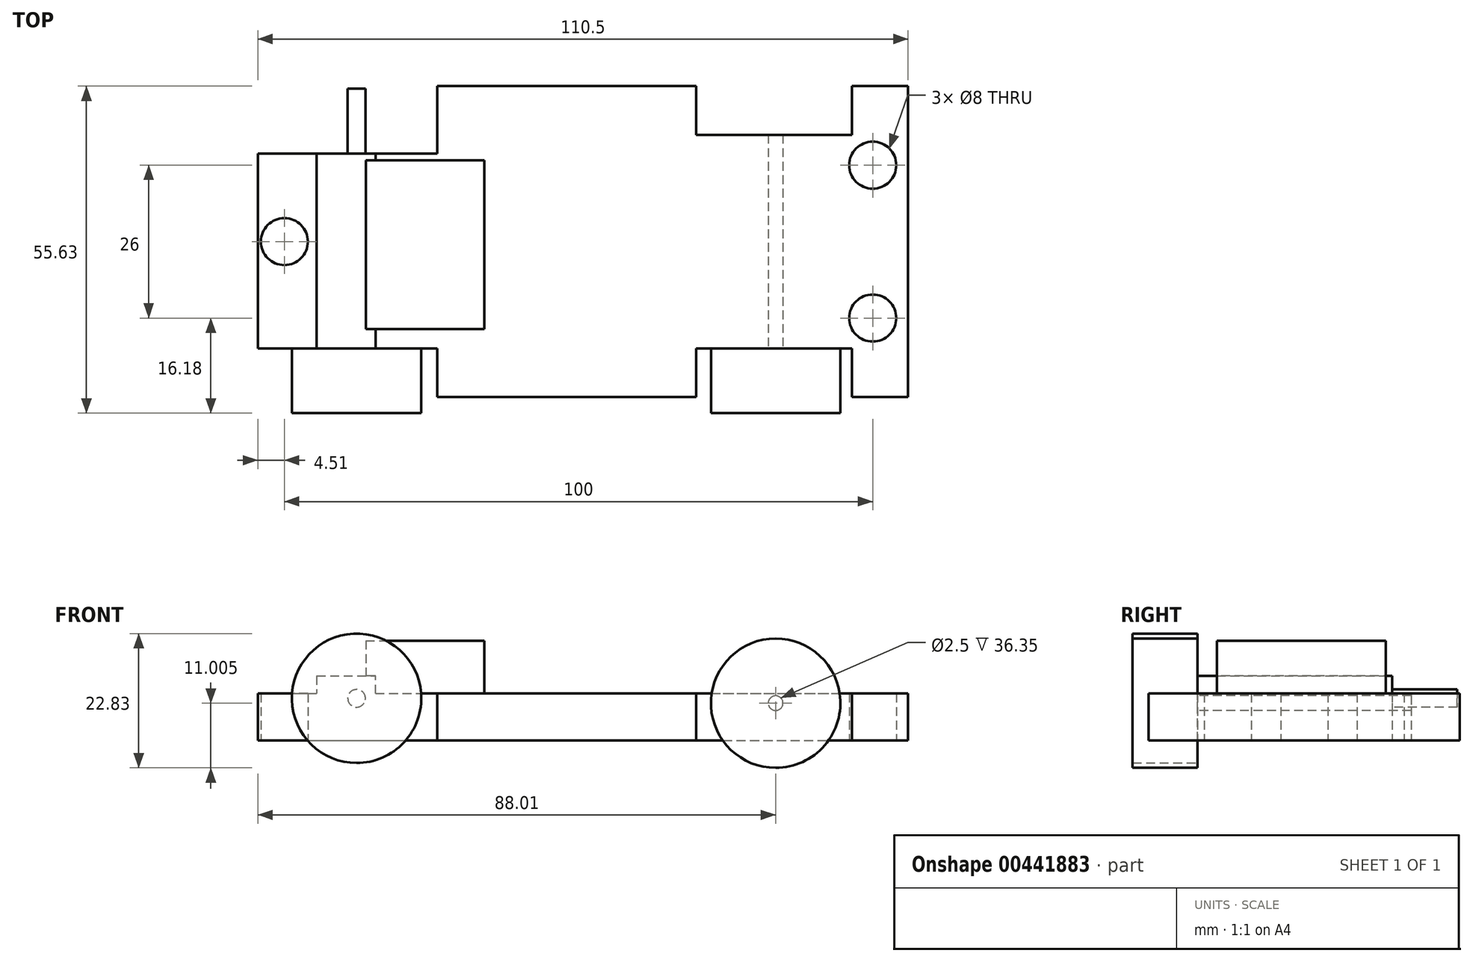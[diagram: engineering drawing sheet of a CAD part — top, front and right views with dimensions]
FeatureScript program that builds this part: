
annotation { "Feature Type Name" : "Feature", "Feature Type Description" : "" }
export const myFeature = defineFeature(function(context is Context, id is Id, definition is map)
    precondition{}
    {
        {
            var Q0;
            Q0=qCreatedBy(makeId("Top.planeOp"),FACE);
            var sketch = newSketch(context, id + "F0", { "sketchPlane" : qUnion([Q0])});
            skLineSegment(sketch, "E0.bottom", {"start": v(55.25, 26.46) * mm, "end": v(45.74, 26.46) * mm});
            skLineSegment(sketch, "E0.top", {"start": v(55.25, -26.46) * mm, "end": v(45.74, -26.46) * mm});
            skLineSegment(sketch, "E0.left", {"start": v(55.25, 26.46) * mm, "end": v(55.25, -26.46) * mm});
            skLineSegment(sketch, "E0.right", {"start": v(-55.25, 14.95) * mm, "end": v(-55.25, -18.18) * mm});
            skPoint(sketch, "E0.middle", {"position": v(0, 0) * mm});
            skCircle(sketch, "E1", {"center": v(-50.74, 0) * mm, "radius": 4 * mm});
            skCircle(sketch, "E2", {"center": v(49.26, 13) * mm, "radius": 4 * mm});
            skCircle(sketch, "E3.MirrorC", {"center": v(49.26, -13) * mm, "radius": 4 * mm});
            skLineSegment(sketch, "E4.top", {"start": v(-55.25, 14.95) * mm, "end": v(-24.73, 14.96) * mm});
            skLineSegment(sketch, "E4.right", {"start": v(-24.73, 26.45) * mm, "end": v(-24.73, 14.96) * mm});
            skLineSegment(sketch, "E5.top", {"start": v(-55.25, -18.18) * mm, "end": v(-24.75, -18.18) * mm});
            skLineSegment(sketch, "E5.right", {"start": v(-24.75, -26.46) * mm, "end": v(-24.75, -18.18) * mm});
            skLineSegment(sketch, "E6.top", {"start": v(19.25, 18.18) * mm, "end": v(45.74, 18.18) * mm});
            skLineSegment(sketch, "E6.left", {"start": v(19.25, 26.46) * mm, "end": v(19.25, 18.18) * mm});
            skLineSegment(sketch, "E6.right", {"start": v(45.74, 26.46) * mm, "end": v(45.74, 18.18) * mm});
            skLineSegment(sketch, "E7.MirrorCS", {"start": v(19.25, -18.18) * mm, "end": v(45.74, -18.18) * mm});
            skLineSegment(sketch, "E8.MirrorCS", {"start": v(19.25, -26.46) * mm, "end": v(19.25, -18.18) * mm});
            skLineSegment(sketch, "E9.MirrorCS", {"start": v(45.74, -26.46) * mm, "end": v(45.74, -18.18) * mm});
            skPoint(sketch, "E10.orphan", {"position": v(-55.25, 26.46) * mm});
            skPoint(sketch, "E11.orphan", {"position": v(-55.25, -26.46) * mm});
            skLineSegment(sketch, "E12.trimOffspring", {"start": v(19.25, -26.46) * mm, "end": v(-24.75, -26.46) * mm});
            skLineSegment(sketch, "E13.trimOffspring", {"start": v(19.25, 26.46) * mm, "end": v(-24.73, 26.46) * mm});
            skSolve(sketch);
        }
        {
            var Q0;
            Q0=qSketchRegion(id+"F0",true);
            extrude(context, id + "F1", {"entities" : qUnion([Q0]), "depth" : 8 * mm});
        }
        {
            var Q0;
            Q0=makeQuery(id+"F1.opExtrude","CAP_FACE",FACE,{"disambiguationData":[OSD([sQuery(id+"F0.wireOp",EDGE,"E0.bottom"),sQuery(id+"F0.wireOp",EDGE,"E0.top"),sQuery(id+"F0.wireOp",EDGE,"E0.left"),sQuery(id+"F0.wireOp",EDGE,"E0.right"),sQuery(id+"F0.wireOp",EDGE,"E1"),sQuery(id+"F0.wireOp",EDGE,"E2"),sQuery(id+"F0.wireOp",EDGE,"E3.MirrorC"),sQuery(id+"F0.wireOp",EDGE,"E4.top"),sQuery(id+"F0.wireOp",EDGE,"E4.right"),sQuery(id+"F0.wireOp",EDGE,"E5.top"),sQuery(id+"F0.wireOp",EDGE,"E5.right"),sQuery(id+"F0.wireOp",EDGE,"E6.top"),sQuery(id+"F0.wireOp",EDGE,"E6.left"),sQuery(id+"F0.wireOp",EDGE,"E6.right"),sQuery(id+"F0.wireOp",EDGE,"E7.MirrorCS"),sQuery(id+"F0.wireOp",EDGE,"E8.MirrorCS"),sQuery(id+"F0.wireOp",EDGE,"E9.MirrorCS"),sQuery(id+"F0.wireOp",EDGE,"E12.trimOffspring"),sQuery(id+"F0.wireOp",EDGE,"E13.trimOffspring")])],"isStart":false});
            var sketch = newSketch(context, id + "F2", { "sketchPlane" : qUnion([Q0])});
            skLineSegment(sketch, "E14.bottom", {"start": v(-45.25, 14.95) * mm, "end": v(-35.25, 14.96) * mm});
            skLineSegment(sketch, "E14.top", {"start": v(-45.25, -18.18) * mm, "end": v(-35.25, -18.18) * mm});
            skLineSegment(sketch, "E14.left", {"start": v(-45.25, 14.95) * mm, "end": v(-45.25, -18.18) * mm});
            skLineSegment(sketch, "E14.right", {"start": v(-35.25, 14.96) * mm, "end": v(-35.25, -18.18) * mm});
            skSolve(sketch);
        }
        {
            var Q0;
            Q0=qSketchRegion(id+"F2",true);
            extrude(context, id + "F3", {"entities" : qUnion([Q0]), "operationType" : NewBodyOperationType.ADD, "depth" : 3 * mm});
        }
        {
            var Q0;
            Q0=qCreatedBy(makeId("Front.planeOp"),FACE);
            var sketch = newSketch(context, id + "F4", { "sketchPlane" : qUnion([Q0])});
            skCircle(sketch, "E15", {"center": v(-38.47, 7.2) * mm, "radius": 1.5 * mm});
            skSolve(sketch);
        }
        {
            var Q0;
            Q0=qSketchRegion(id+"F4",true);
            extrude(context, id + "F5", {"entities" : qUnion([Q0]), "operationType" : NewBodyOperationType.ADD, "endBound" : BoundingType.SYMMETRIC, "oppositeDirection" : true, "depth" : 52 * mm});
        }
        {
            var Q0;
            {var subQ0=sQuery(id+"F0.wireOp",EDGE,"E6.top");var subQ1=sQuery(id+"F0.wireOp",EDGE,"E12.trimOffspring");var subQ2=sQuery(id+"F0.wireOp",EDGE,"E13.trimOffspring");var subQ3=sQuery(id+"F0.wireOp",EDGE,"E5.right");var subQ4=sQuery(id+"F0.wireOp",EDGE,"E5.top");var subQ5=sQuery(id+"F0.wireOp",EDGE,"E9.MirrorCS");var subQ6=sQuery(id+"F0.wireOp",EDGE,"E4.top");var subQ7=sQuery(id+"F0.wireOp",EDGE,"E7.MirrorCS");var subQ8=sQuery(id+"F0.wireOp",EDGE,"E3.MirrorC");var subQ9=sQuery(id+"F0.wireOp",EDGE,"E0.bottom");var subQ10=sQuery(id+"F0.wireOp",EDGE,"E4.right");var subQ11=sQuery(id+"F0.wireOp",EDGE,"E8.MirrorCS");var subQ12=sQuery(id+"F0.wireOp",EDGE,"E0.top");var subQ13=sQuery(id+"F0.wireOp",EDGE,"E0.left");var subQ14=sQuery(id+"F0.wireOp",EDGE,"E2");var subQ15=sQuery(id+"F0.wireOp",EDGE,"E6.left");var subQ16=sQuery(id+"F0.wireOp",EDGE,"E6.right");Q0=makeQuery(id+"F3.boolean.opBoolean","SPLIT",FACE,{"disambiguationData":[TD([makeQuery(id+"F1.opExtrude","SWEPT_FACE",FACE,{"disambiguationData":[OSD([subQ9])]})])],"derivedFrom":makeQuery(id+"F1.opExtrude","CAP_FACE",FACE,{"disambiguationData":[OSD([subQ9,subQ12,subQ13,sQuery(id+"F0.wireOp",EDGE,"E0.right"),sQuery(id+"F0.wireOp",EDGE,"E1"),subQ14,subQ8,subQ6,subQ10,subQ4,subQ3,subQ0,subQ15,subQ16,subQ7,subQ11,subQ5,subQ1,subQ2])],"isStart":false})});}
            var sketch = newSketch(context, id + "F6", { "sketchPlane" : qUnion([Q0])});
            skLineSegment(sketch, "E16.bottom", {"start": v(-36.9, 13.86) * mm, "end": v(-16.75, 13.86) * mm});
            skLineSegment(sketch, "E16.top", {"start": v(-36.9, -14.86) * mm, "end": v(-16.75, -14.86) * mm});
            skLineSegment(sketch, "E16.left", {"start": v(-36.9, 13.86) * mm, "end": v(-36.9, -14.86) * mm});
            skLineSegment(sketch, "E16.right", {"start": v(-16.75, 13.86) * mm, "end": v(-16.75, -14.86) * mm});
            skSolve(sketch);
        }
        {
            var Q0;
            Q0=qSketchRegion(id+"F6",true);
            extrude(context, id + "F7", {"entities" : qUnion([Q0]), "operationType" : NewBodyOperationType.ADD, "depth" : 9 * mm});
        }
        {
            var Q0;
            Q0=makeQuery(id+"F3.boolean.opBoolean","MERGE",FACE,{"derivedFrom":[makeQuery(id+"F1.opExtrude","SWEPT_FACE",FACE,{"disambiguationData":[OSD([sQuery(id+"F0.wireOp",EDGE,"E5.top")])]}),makeQuery(id+"F3.opExtrude","SWEPT_FACE",FACE,{"disambiguationData":[OSD([sQuery(id+"F2.wireOp",EDGE,"E14.top")])]})]});
            var sketch = newSketch(context, id + "F8", { "sketchPlane" : qUnion([Q0])});
            skCircle(sketch, "E17", {"center": v(-38.47, 7.2) * mm, "radius": 11 * mm});
            skSolve(sketch);
        }
        {
            var Q0;
            Q0=qSketchRegion(id+"F8",true);
            extrude(context, id + "F9", {"entities" : qUnion([Q0]), "operationType" : NewBodyOperationType.ADD, "depth" : 11 * mm});
        }
        {
            var Q0;
            Q0=makeQuery(id+"F1.opExtrude","SWEPT_FACE",FACE,{"disambiguationData":[OSD([sQuery(id+"F0.wireOp",EDGE,"E7.MirrorCS")])]});
            var sketch = newSketch(context, id + "F10", { "sketchPlane" : qUnion([Q0])});
            skCircle(sketch, "E18", {"center": v(32.76, 6.38) * mm, "radius": 1.25 * mm});
            skSolve(sketch);
        }
        {
            var Q0;
            Q0=qSketchRegion(id+"F10",true);
            extrude(context, id + "F11", {"entities" : qUnion([Q0]), "operationType" : NewBodyOperationType.REMOVE, "endBound" : BoundingType.THROUGH_ALL, "oppositeDirection" : true, "depth" : 25 * mm});
        }
        {
            var Q0;
            Q0=makeQuery(id+"F1.opExtrude","SWEPT_FACE",FACE,{"disambiguationData":[OSD([sQuery(id+"F0.wireOp",EDGE,"E7.MirrorCS")])]});
            var sketch = newSketch(context, id + "F12", { "sketchPlane" : qUnion([Q0])});
            skCircle(sketch, "E19", {"center": v(32.76, 6.38) * mm, "radius": 11 * mm});
            skSolve(sketch);
        }
        {
            var Q0;
            Q0=qSketchRegion(id+"F12",true);
            extrude(context, id + "F13", {"entities" : qUnion([Q0]), "operationType" : NewBodyOperationType.ADD, "depth" : 11 * mm});
        }
    });
